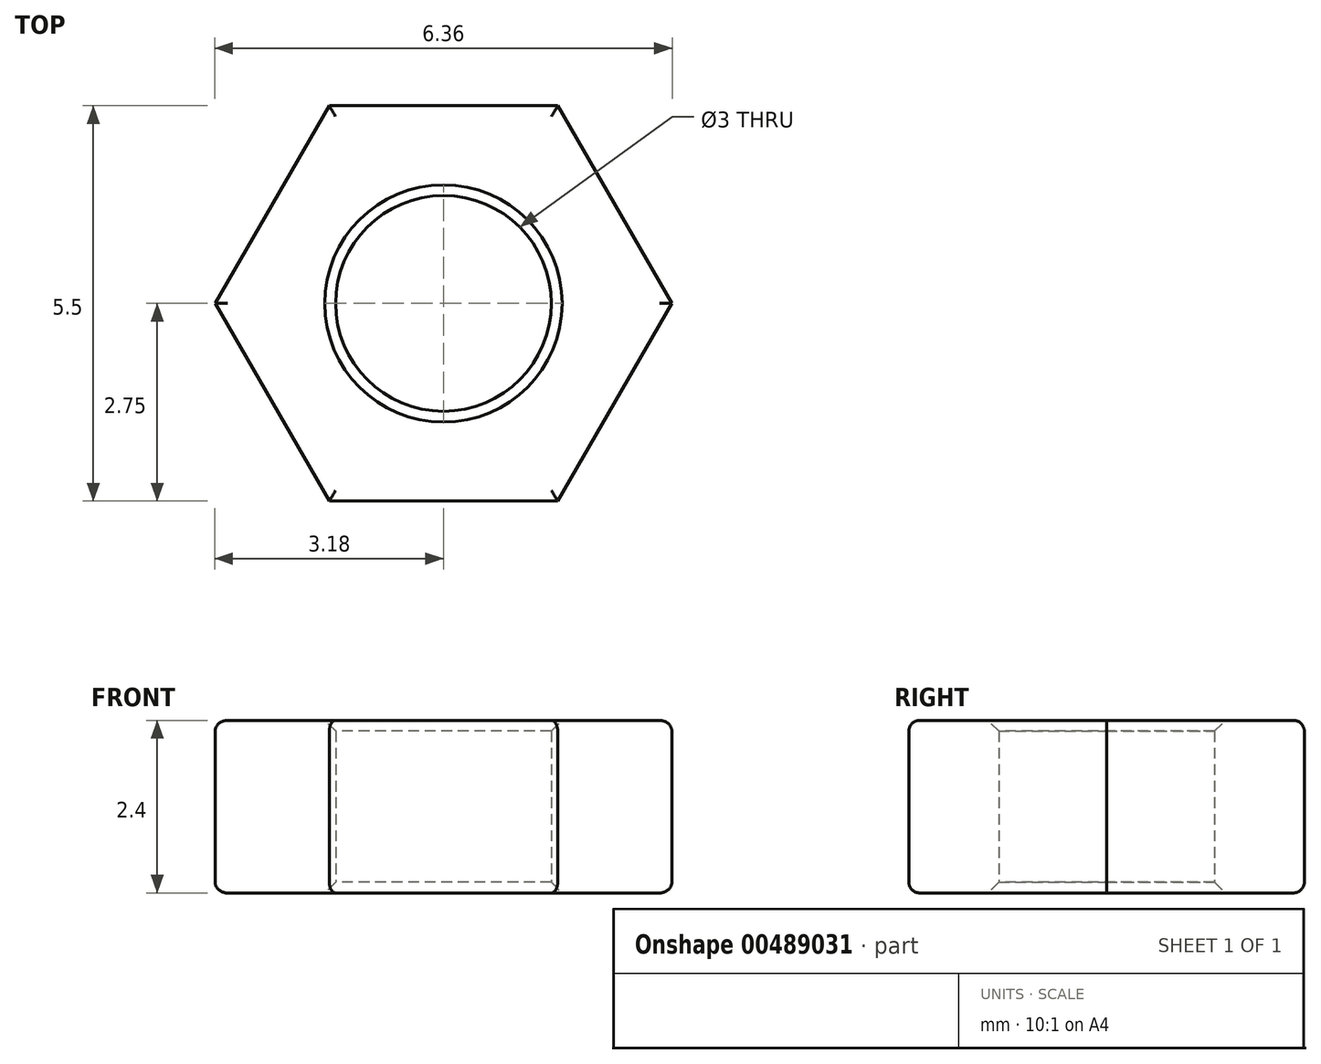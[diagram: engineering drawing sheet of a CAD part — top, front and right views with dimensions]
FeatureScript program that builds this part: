
annotation { "Feature Type Name" : "Feature", "Feature Type Description" : "" }
export const myFeature = defineFeature(function(context is Context, id is Id, definition is map)
    precondition{}
    {
        {
            assignVariable(context, id + "F0", {"name" : "d", "anyValue" : 3});
        }
        {
            assignVariable(context, id + "F1", {"name" : "L", "anyValue" : 2.4});
        }
        {
            var Q0;
            Q0=qCreatedBy(makeId("Top.planeOp"),FACE);
            var sketch = newSketch(context, id + "F2", { "sketchPlane" : qUnion([Q0])});
            skCircle(sketch, "E0", {"center": v(0, 0) * mm, "radius": 1.5 * mm});
            skCircle(sketch, "E1.cCircle", {"center": v(0, 0) * mm, "radius": 2.75 * mm, "construction": true});
            skLineSegment(sketch, "E1.0", {"start": v(-1.59, 2.75) * mm, "end": v(1.59, 2.75) * mm});
            skLineSegment(sketch, "E1.1", {"start": v(1.59, 2.75) * mm, "end": v(3.18, 0) * mm});
            skLineSegment(sketch, "E1.2", {"start": v(3.18, 0) * mm, "end": v(1.59, -2.75) * mm});
            skLineSegment(sketch, "E1.3", {"start": v(1.59, -2.75) * mm, "end": v(-1.59, -2.75) * mm});
            skLineSegment(sketch, "E1.4", {"start": v(-1.59, -2.75) * mm, "end": v(-3.18, 0) * mm});
            skLineSegment(sketch, "E1.5", {"start": v(-3.18, 0) * mm, "end": v(-1.59, 2.75) * mm});
            skPoint(sketch, "E1.0.midPoint", {"position": v(0, 2.75) * mm});
            skSolve(sketch);
        }
        {
            var Q0;
            Q0=qSketchRegion(id+"F2",true);
            extrude(context, id + "F3", {"entities" : qUnion([Q0]), "depth" : (getVariable(context, 'L')) * mm});
        }
        {
            var Q0;
            Q0=makeQuery(id+"F3.opExtrude","CAP_EDGE",EDGE,{"disambiguationData":[OSD([sQuery(id+"F2.wireOp",EDGE,"E1.2")])],"isStart":false});
            var Q1;
            Q1=makeQuery(id+"F3.opExtrude","CAP_EDGE",EDGE,{"disambiguationData":[OSD([sQuery(id+"F2.wireOp",EDGE,"E1.1")])],"isStart":false});
            var Q2;
            Q2=makeQuery(id+"F3.opExtrude","CAP_EDGE",EDGE,{"disambiguationData":[OSD([sQuery(id+"F2.wireOp",EDGE,"E1.0")])],"isStart":false});
            var Q3;
            Q3=makeQuery(id+"F3.opExtrude","CAP_EDGE",EDGE,{"disambiguationData":[OSD([sQuery(id+"F2.wireOp",EDGE,"E1.5")])],"isStart":false});
            var Q4;
            Q4=makeQuery(id+"F3.opExtrude","CAP_EDGE",EDGE,{"disambiguationData":[OSD([sQuery(id+"F2.wireOp",EDGE,"E1.4")])],"isStart":false});
            var Q5;
            Q5=makeQuery(id+"F3.opExtrude","CAP_EDGE",EDGE,{"disambiguationData":[OSD([sQuery(id+"F2.wireOp",EDGE,"E1.3")])],"isStart":false});
            var Q6;
            Q6=makeQuery(id+"F3.opExtrude","CAP_EDGE",EDGE,{"disambiguationData":[OSD([sQuery(id+"F2.wireOp",EDGE,"E1.3")])],"isStart":true});
            var Q7;
            Q7=makeQuery(id+"F3.opExtrude","CAP_EDGE",EDGE,{"disambiguationData":[OSD([sQuery(id+"F2.wireOp",EDGE,"E1.2")])],"isStart":true});
            var Q8;
            Q8=makeQuery(id+"F3.opExtrude","CAP_EDGE",EDGE,{"disambiguationData":[OSD([sQuery(id+"F2.wireOp",EDGE,"E1.4")])],"isStart":true});
            var Q9;
            Q9=makeQuery(id+"F3.opExtrude","CAP_EDGE",EDGE,{"disambiguationData":[OSD([sQuery(id+"F2.wireOp",EDGE,"E1.5")])],"isStart":true});
            var Q10;
            Q10=makeQuery(id+"F3.opExtrude","CAP_EDGE",EDGE,{"disambiguationData":[OSD([sQuery(id+"F2.wireOp",EDGE,"E1.0")])],"isStart":true});
            var Q11;
            Q11=makeQuery(id+"F3.opExtrude","CAP_EDGE",EDGE,{"disambiguationData":[OSD([sQuery(id+"F2.wireOp",EDGE,"E1.1")])],"isStart":true});
            fillet(context, id + "F4", {"entities" : qUnion([Q0, Q1, Q2, Q3, Q4, Q5, Q6, Q7, Q8, Q9, Q10, Q11]), "radius" : (getVariable(context, 'd') / 20) * mm, "tangentPropagation" : true, "allowEdgeOverflow" : false});
        }
        {
            var Q0;
            Q0=makeQuery(id+"F3.opExtrude","CAP_EDGE",EDGE,{"disambiguationData":[OSD([sQuery(id+"F2.wireOp",EDGE,"E0")])],"isStart":false});
            var Q1;
            Q1=makeQuery(id+"F3.opExtrude","CAP_EDGE",EDGE,{"disambiguationData":[OSD([sQuery(id+"F2.wireOp",EDGE,"E0")])],"isStart":true});
            chamfer(context, id + "F5", {"entities" : qUnion([Q0, Q1]), "width" : (getVariable(context, 'd') / 20) * mm, "tangentPropagation" : true});
        }
    });
